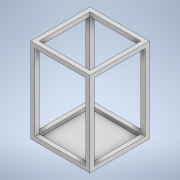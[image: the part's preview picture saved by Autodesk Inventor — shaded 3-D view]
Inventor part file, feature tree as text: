
AUTODESK INVENTOR PART (.ipt)
format: ipt  version: 2022 (Build 260153000, 153)  size: 168,448 bytes
history: native  units: mm
features: sketch x8, extrude x7
ambient origin geometry x8: Origin, YZ Plane, XZ Plane, XY Plane, X Axis, Y Axis, Z Axis, Center Point
bodies: Solid1 (feature_tree)
feature tree (15):
  sketch  "Sketch1"  dims[d0=600.0mm d1=600.0mm]
  sketch  "Sketch2"  dims[d2=700.0mm d3=700.0mm]
  extrude  "Extrusion1"  Depth=600.0mm
  extrude  "Extrusion2"  Depth=700.0mm
  extrude  "Extrusion3"  Depth=50.0mm TaperAngle=0.0deg
  sketch  "3D Sketch1"
  sketch  "Sketch3"  dims[d4=10.0mm d5=0.0mm d6=50.0mm d7=0.0mm]
  sketch  "Sketch4"  dims[d8=1000.0mm d9=0.0mm d13=50.0mm]
  extrude  "Extrusion4"  Depth=50.0mm
  extrude  "Extrusion5"  Depth=10.0mm TaperAngle=0.0deg
  extrude  "Extrusion6"  Depth=10.0mm TaperAngle=0.0deg
  extrude  "Extrusion7"  [1 undecoded]
  sketch  "Sketch5"  dims[d14=10.0mm d15=0.0mm d16=10.0mm d17=0.0mm]
  sketch  "Sketch6"  dims[d18=50.0mm d19=10.0mm d20=0.0mm]
  sketch  "Sketch7"  dims[d21=10.0mm d22=0.0mm]
note: 1 required parameter value undecoded (feature->parameter linkage not recoverable at this tier; creation-order binding heuristic only, values carry confidence <= 0.55)
